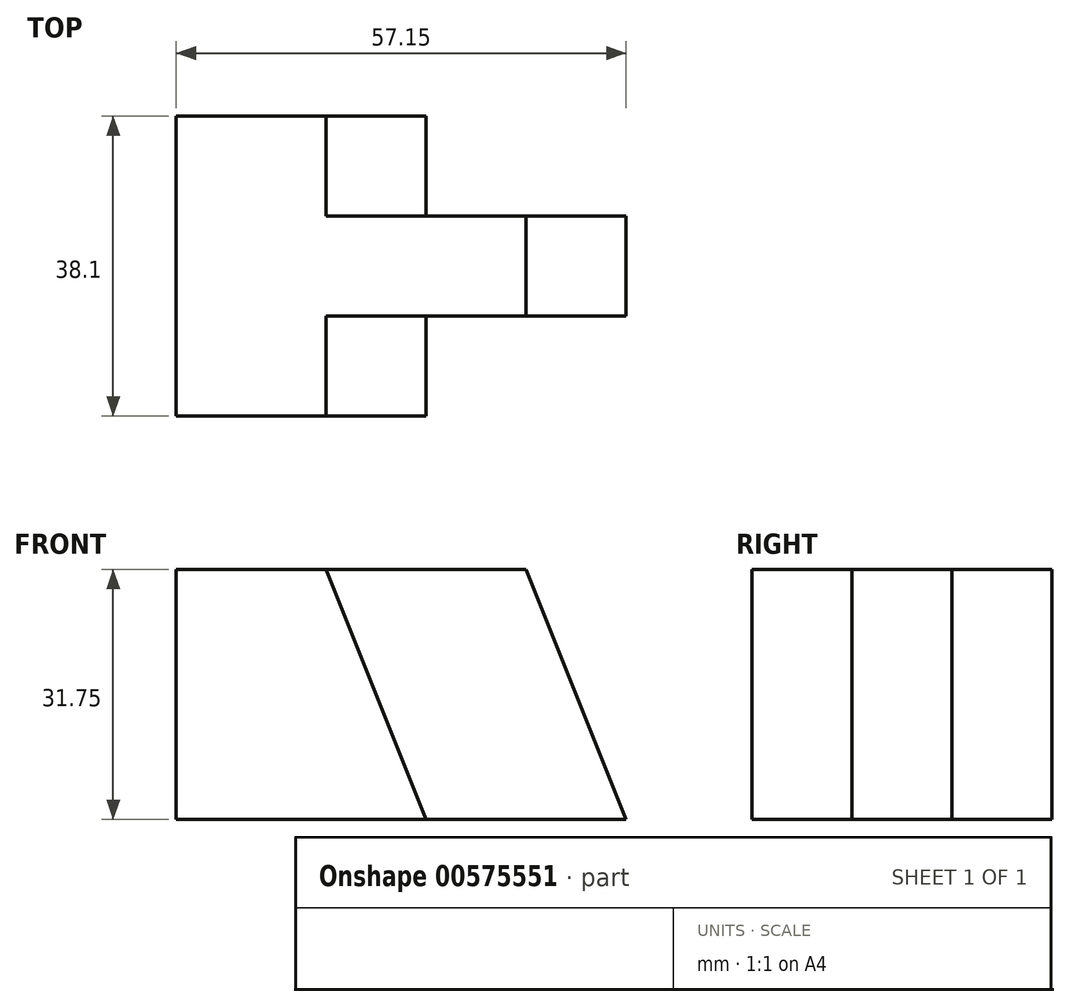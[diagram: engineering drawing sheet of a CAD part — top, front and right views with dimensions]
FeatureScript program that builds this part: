
annotation { "Feature Type Name" : "Feature", "Feature Type Description" : "" }
export const myFeature = defineFeature(function(context is Context, id is Id, definition is map)
    precondition{}
    {
        {
            var Q0;
            Q0=qCreatedBy(makeId("Front.planeOp"),FACE);
            var sketch = newSketch(context, id + "F0", { "sketchPlane" : qUnion([Q0])});
            skLineSegment(sketch, "E0", {"start": v(0, 0) * mm, "end": v(57.15, 0) * mm});
            skLineSegment(sketch, "E1", {"start": v(0, 0) * mm, "end": v(0, 31.75) * mm});
            skLineSegment(sketch, "E2", {"start": v(0, 31.75) * mm, "end": v(44.45, 31.75) * mm});
            skLineSegment(sketch, "E3", {"start": v(44.45, 31.75) * mm, "end": v(57.15, 0) * mm});
            skSolve(sketch);
        }
        {
            var Q0;
            Q0=qSketchRegion(id+"F0",true);
            extrude(context, id + "F1", {"entities" : qUnion([Q0]), "depth" : 12.7 * mm, "offsetDistance" : 25.4 * mm});
        }
        {
            var Q0;
            Q0=qCreatedBy(makeId("Front.planeOp"),FACE);
            var sketch = newSketch(context, id + "F2", { "sketchPlane" : qUnion([Q0])});
            skLineSegment(sketch, "E4", {"start": v(0, 0) * mm, "end": v(31.75, 0) * mm});
            skLineSegment(sketch, "E5", {"start": v(0, 0) * mm, "end": v(0, 31.75) * mm});
            skLineSegment(sketch, "E6", {"start": v(0, 31.75) * mm, "end": v(19.05, 31.75) * mm});
            skLineSegment(sketch, "E7", {"start": v(19.05, 31.75) * mm, "end": v(31.75, 0) * mm});
            skSolve(sketch);
        }
        {
            var Q0;
            Q0=qSketchRegion(id+"F2",true);
            extrude(context, id + "F3", {"entities" : qUnion([Q0]), "operationType" : NewBodyOperationType.ADD, "depth" : 25.4 * mm, "offsetDistance" : 25.4 * mm});
        }
        {
            var Q0;
            Q0=qCreatedBy(makeId("Front.planeOp"),FACE);
            var sketch = newSketch(context, id + "F4", { "sketchPlane" : qUnion([Q0])});
            skLineSegment(sketch, "E8", {"start": v(0, 0) * mm, "end": v(0, 31.75) * mm});
            skLineSegment(sketch, "E9", {"start": v(0, 31.75) * mm, "end": v(19.05, 31.75) * mm});
            skLineSegment(sketch, "E10", {"start": v(0, 0) * mm, "end": v(31.75, 0) * mm});
            skLineSegment(sketch, "E11", {"start": v(31.75, 0) * mm, "end": v(19.05, 31.75) * mm});
            skSolve(sketch);
        }
        {
            var Q0;
            Q0=qSketchRegion(id+"F4",true);
            extrude(context, id + "F5", {"entities" : qUnion([Q0]), "operationType" : NewBodyOperationType.ADD, "oppositeDirection" : true, "depth" : 12.7 * mm, "offsetDistance" : 25.4 * mm});
        }
    });
